# Revit family: Netto LED - Generic
name_source: partatom
category: Lighting Fixtures
revit_build: Autodesk Revit Architecture 2014 (Build: 20140709_2115(x64)
units: mm (PartAtom-declared; Revit-internal decimal feet)

## types (1)
- Netto LED
    Apparent Load = 240 VA
    ArticleNumber = See URL hyperlink
    AssetType = Moveable/Fixed
    BIMObjectName = Netto LED.rfa
    BSAB 96 = SNB.2
    BallastsCELMAEnergyEfficiencyIndex = Class A1/A2
    CCSClassCode = UAC
    CCSClassName = Belysningsarmatur
    CCSTopnode = L
    Colour = White
    ControlGearPosition = Integrated
    Description = 70-80-35 General Lighting Systems
    DocumentReference = See URL hyperlink
    Documentation = See URL hyperlink
    Emit from Line Length = 1500 mm
    Finish = Powder coated
    Frame Depth = 230 mm
    Frame Width = 1530 mm
    HasProtectiveEarth = TRUE
    Height 1 = 85 mm
    IP_Code = IP20
    IfcExportAs = IfcLightFixtureType'
    IfcExportType = NOTDEFINED'
    InsulationStandardClass = Class 1
    InternalFuse = Only required in emergency versions
    LampColourRenderingIndex = Ra>80 (Ra>90 on request)
    LampRating = 55W
    LampType = LED
    Light Source Definition (family) = Line+HemiSpherical
    Light Source Symbol Size = 610 mm
    LightFixtureMountingType = Surface
    LightFixturePlacingType = Ceiling
    LightSource = LED 3000K (4000K on request)
    LuminairePowerFactor = >0,9
    LuminaireType = Direct LED Luminaire
    Manufacturer = Riegens A/S
    ManufacturerURL = www.riegens.com
    Material = Steel and Acrylic (PMMA)
    Model = Netto LED
    ModelReference = Netto LED
    NominalVoltage = 220-240V
    OmniClass Number = 23.80.70.11
    OmniClass Title = Luminaries for Internal Lighting
    Optic = Direct: White steel reflector and opal diffuser
    PhaseReference = IEC recommendations
    PhotometricPerformance = In accordance with BS EN 13032-1
    ProductInformation = http://riegens.com
    Shape = Rectangle
    Size = 230 x 1530 x 85 mm
    TotalWattage = Max. 60W
    URL = http://riegens.com
    Uniclass 1.4 = JY73
    Uniclass2 = Pr_70_70_49_43 Light-Emitting Diode (LED) Luminaires
    Version = v.1.0

## geometry (parser evidence)
native form markers: Sweep x4
no freeform markers — native parametric forms only
